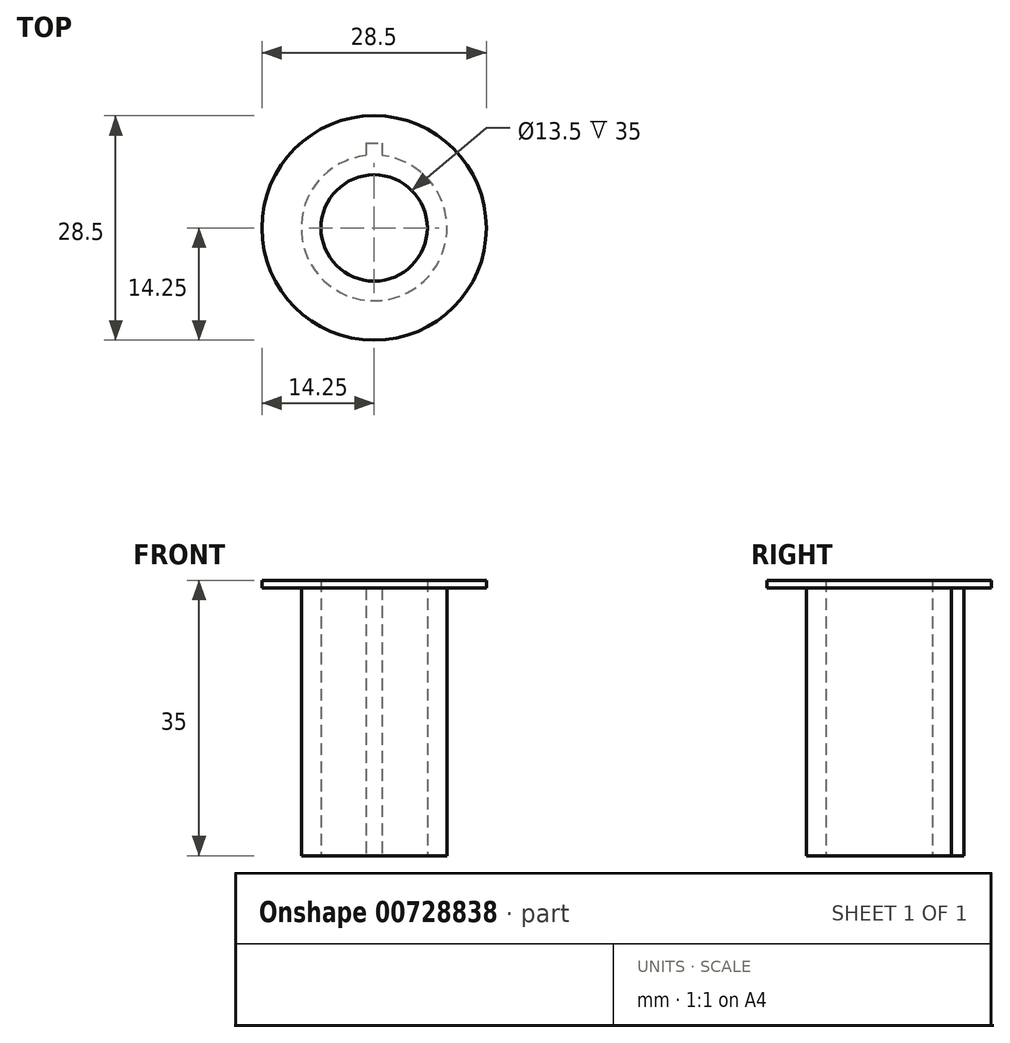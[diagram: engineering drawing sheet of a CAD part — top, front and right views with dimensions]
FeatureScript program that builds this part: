
annotation { "Feature Type Name" : "Feature", "Feature Type Description" : "" }
export const myFeature = defineFeature(function(context is Context, id is Id, definition is map)
    precondition{}
    {
        {
            var Q0;
            Q0=qCreatedBy(makeId("Top.planeOp"),FACE);
            var sketch = newSketch(context, id + "F0", { "sketchPlane" : qUnion([Q0])});
            skCircle(sketch, "E0", {"center": v(0, 0) * mm, "radius": 6.75 * mm});
            skCircle(sketch, "E1", {"center": v(0, 0) * mm, "radius": 9.25 * mm});
            skSolve(sketch);
        }
        {
            var Q0;
            Q0=qSketchRegion(id+"F0",true);
            extrude(context, id + "F1", {"entities" : qUnion([Q0]), "depth" : 35 * mm, "offsetDistance" : 25 * mm});
        }
        {
            var Q0;
            Q0=makeQuery(id+"F1.opExtrude","CAP_FACE",FACE,{"disambiguationData":[OSD([sQuery(id+"F0.wireOp",EDGE,"E0"),sQuery(id+"F0.wireOp",EDGE,"E1")])],"isStart":false});
            var sketch = newSketch(context, id + "F2", { "sketchPlane" : qUnion([Q0])});
            skLineSegment(sketch, "E2.bottom", {"start": v(1, 7.75) * mm, "end": v(-1, 7.75) * mm});
            skLineSegment(sketch, "E2.top", {"start": v(1, 10.75) * mm, "end": v(-1, 10.75) * mm});
            skLineSegment(sketch, "E2.left", {"start": v(1, 7.75) * mm, "end": v(1, 10.75) * mm});
            skLineSegment(sketch, "E2.right", {"start": v(-1, 7.75) * mm, "end": v(-1, 10.75) * mm});
            skPoint(sketch, "E2.middle", {"position": v(0, 9.25) * mm});
            skSolve(sketch);
        }
        {
            var Q0;
            Q0=qSketchRegion(id+"F2",true);
            extrude(context, id + "F3", {"entities" : qUnion([Q0]), "operationType" : NewBodyOperationType.ADD, "oppositeDirection" : true, "depth" : 35 * mm, "offsetDistance" : 25 * mm});
        }
        {
            var Q0;
            {var subQ0=sQuery(id+"F2.wireOp",EDGE,"E2.right");var subQ1=sQuery(id+"F2.wireOp",EDGE,"E2.left");var subQ2=sQuery(id+"F2.wireOp",EDGE,"E2.top");var subQ3=sQuery(id+"F2.wireOp",EDGE,"E2.bottom");Q0=makeQuery(id+"Fw7L3IugUGlv9Yr_1.13.F3.boolean.opBoolean","MERGE",FACE,{"derivedFrom":[makeQuery(id+"Fw7L3IugUGlv9Yr_1.12.F3.boolean.opBoolean","MERGE",FACE,{"derivedFrom":[makeQuery(id+"Fw7L3IugUGlv9Yr_1.11.F3.boolean.opBoolean","MERGE",FACE,{"derivedFrom":[makeQuery(id+"Fw7L3IugUGlv9Yr_1.10.F3.boolean.opBoolean","MERGE",FACE,{"derivedFrom":[makeQuery(id+"Fw7L3IugUGlv9Yr_1.9.F3.boolean.opBoolean","MERGE",FACE,{"derivedFrom":[makeQuery(id+"Fw7L3IugUGlv9Yr_1.8.F3.boolean.opBoolean","MERGE",FACE,{"derivedFrom":[makeQuery(id+"Fw7L3IugUGlv9Yr_1.7.F3.boolean.opBoolean","MERGE",FACE,{"derivedFrom":[makeQuery(id+"Fw7L3IugUGlv9Yr_1.6.F3.boolean.opBoolean","MERGE",FACE,{"derivedFrom":[makeQuery(id+"Fw7L3IugUGlv9Yr_1.5.F3.boolean.opBoolean","MERGE",FACE,{"derivedFrom":[makeQuery(id+"Fw7L3IugUGlv9Yr_1.4.F3.boolean.opBoolean","MERGE",FACE,{"derivedFrom":[makeQuery(id+"Fw7L3IugUGlv9Yr_1.3.F3.boolean.opBoolean","MERGE",FACE,{"derivedFrom":[makeQuery(id+"Fw7L3IugUGlv9Yr_1.2.F3.boolean.opBoolean","MERGE",FACE,{"derivedFrom":[makeQuery(id+"Fw7L3IugUGlv9Yr_1.1.F3.boolean.opBoolean","MERGE",FACE,{"derivedFrom":[makeQuery(id+"F3.boolean.opBoolean","MERGE",FACE,{"derivedFrom":[makeQuery(id+"F1.opExtrude","CAP_FACE",FACE,{"disambiguationData":[OSD([sQuery(id+"F0.wireOp",EDGE,"E0"),sQuery(id+"F0.wireOp",EDGE,"E1")])],"isStart":false}),makeQuery(id+"F3.opExtrude","CAP_FACE",FACE,{"disambiguationData":[OSD([subQ3,subQ2,subQ1,subQ0])],"isStart":true})]}),makeQuery(id+"Fw7L3IugUGlv9Yr_1.1.F3.opExtrude","CAP_FACE",FACE,{"disambiguationData":[OSD([subQ3,subQ2,subQ1,subQ0])],"isStart":true})]}),makeQuery(id+"Fw7L3IugUGlv9Yr_1.2.F3.opExtrude","CAP_FACE",FACE,{"disambiguationData":[OSD([subQ3,subQ2,subQ1,subQ0])],"isStart":true})]}),makeQuery(id+"Fw7L3IugUGlv9Yr_1.3.F3.opExtrude","CAP_FACE",FACE,{"disambiguationData":[OSD([subQ3,subQ2,subQ1,subQ0])],"isStart":true})]}),makeQuery(id+"Fw7L3IugUGlv9Yr_1.4.F3.opExtrude","CAP_FACE",FACE,{"disambiguationData":[OSD([subQ3,subQ2,subQ1,subQ0])],"isStart":true})]}),makeQuery(id+"Fw7L3IugUGlv9Yr_1.5.F3.opExtrude","CAP_FACE",FACE,{"disambiguationData":[OSD([subQ3,subQ2,subQ1,subQ0])],"isStart":true})]}),makeQuery(id+"Fw7L3IugUGlv9Yr_1.6.F3.opExtrude","CAP_FACE",FACE,{"disambiguationData":[OSD([subQ3,subQ2,subQ1,subQ0])],"isStart":true})]}),makeQuery(id+"Fw7L3IugUGlv9Yr_1.7.F3.opExtrude","CAP_FACE",FACE,{"disambiguationData":[OSD([subQ3,subQ2,subQ1,subQ0])],"isStart":true})]}),makeQuery(id+"Fw7L3IugUGlv9Yr_1.8.F3.opExtrude","CAP_FACE",FACE,{"disambiguationData":[OSD([subQ3,subQ2,subQ1,subQ0])],"isStart":true})]}),makeQuery(id+"Fw7L3IugUGlv9Yr_1.9.F3.opExtrude","CAP_FACE",FACE,{"disambiguationData":[OSD([subQ3,subQ2,subQ1,subQ0])],"isStart":true})]}),makeQuery(id+"Fw7L3IugUGlv9Yr_1.10.F3.opExtrude","CAP_FACE",FACE,{"disambiguationData":[OSD([subQ3,subQ2,subQ1,subQ0])],"isStart":true})]}),makeQuery(id+"Fw7L3IugUGlv9Yr_1.11.F3.opExtrude","CAP_FACE",FACE,{"disambiguationData":[OSD([subQ3,subQ2,subQ1,subQ0])],"isStart":true})]}),makeQuery(id+"Fw7L3IugUGlv9Yr_1.12.F3.opExtrude","CAP_FACE",FACE,{"disambiguationData":[OSD([subQ3,subQ2,subQ1,subQ0])],"isStart":true})]}),makeQuery(id+"Fw7L3IugUGlv9Yr_1.13.F3.opExtrude","CAP_FACE",FACE,{"disambiguationData":[OSD([subQ3,subQ2,subQ1,subQ0])],"isStart":true})]});}
            var sketch = newSketch(context, id + "F4", { "sketchPlane" : qUnion([Q0])});
            skCircle(sketch, "E3", {"center": v(0, 0) * mm, "radius": 6.75 * mm});
            skCircle(sketch, "E4", {"center": v(0, 0) * mm, "radius": 14.25 * mm});
            skSolve(sketch);
        }
        {
            var Q0;
            Q0=qSketchRegion(id+"F4",true);
            extrude(context, id + "F5", {"entities" : qUnion([Q0]), "operationType" : NewBodyOperationType.ADD, "oppositeDirection" : true, "depth" : 1 * mm, "offsetDistance" : 25 * mm});
        }
    });
